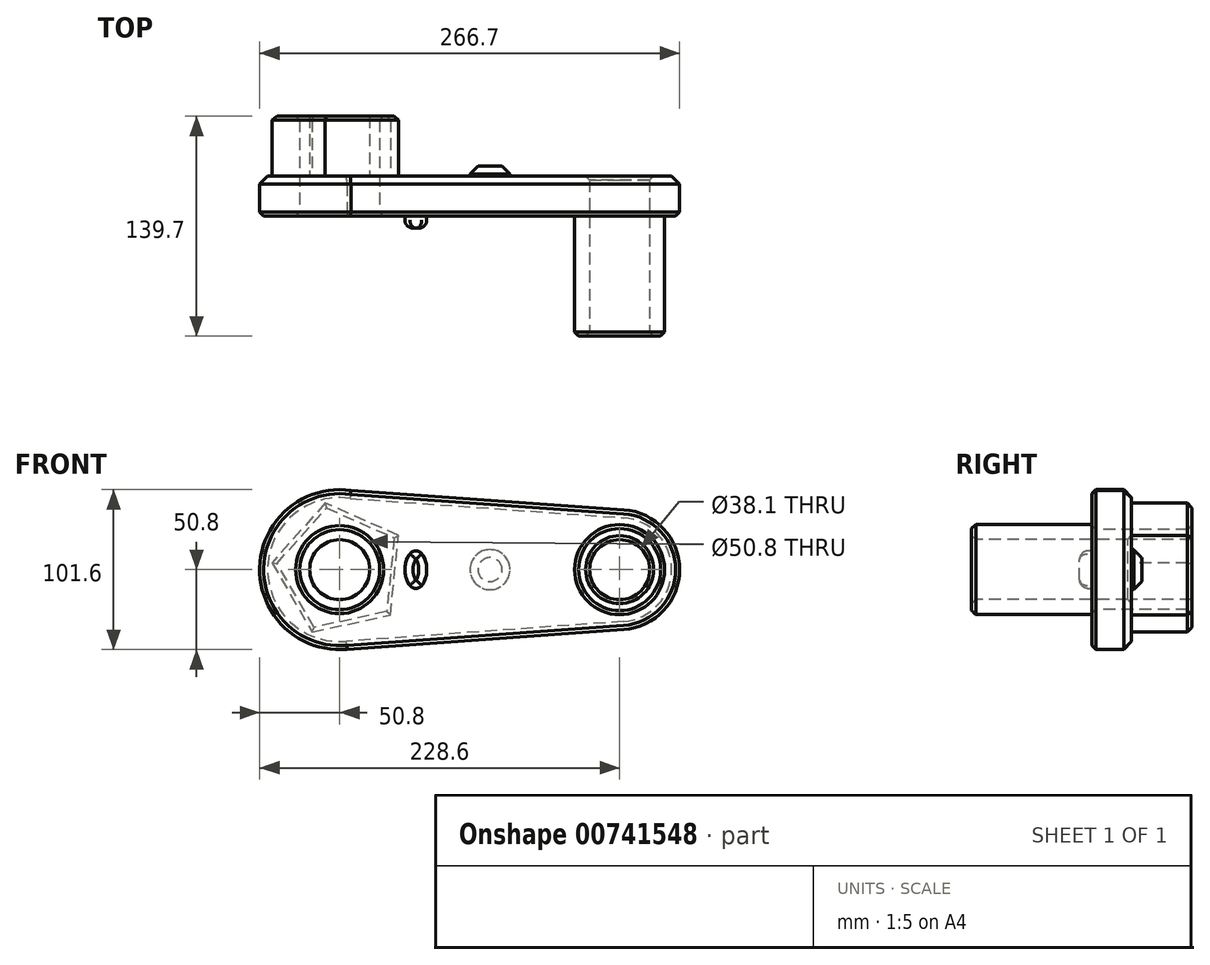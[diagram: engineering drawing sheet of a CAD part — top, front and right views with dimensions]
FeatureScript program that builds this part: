
annotation { "Feature Type Name" : "Feature", "Feature Type Description" : "" }
export const myFeature = defineFeature(function(context is Context, id is Id, definition is map)
    precondition{}
    {
        {
            var Q0;
            Q0=qCreatedBy(makeId("Front.planeOp"),FACE);
            var sketch = newSketch(context, id + "F0", { "sketchPlane" : qUnion([Q0])});
            skCircle(sketch, "E0", {"center": v(0, 0) * mm, "radius": 50.8 * mm});
            skCircle(sketch, "E1", {"center": v(177.8, 0) * mm, "radius": 38.1 * mm});
            skCircle(sketch, "E2", {"center": v(0, 0) * mm, "radius": 25.4 * mm});
            skCircle(sketch, "E3", {"center": v(177.8, 0) * mm, "radius": 19.05 * mm});
            skLineSegment(sketch, "E4", {"start": v(0, 50.8) * mm, "end": v(180.5, 38) * mm});
            skLineSegment(sketch, "E5", {"start": v(4.76, -50.58) * mm, "end": v(180.52, -38) * mm});
            skSolve(sketch);
        }
        {
            var Q0;
            Q0 = qSketchRegion(id + "F0", true);
            extrude(context, id + "F1", {"entities" : qUnion([Q0]), "oppositeDirection" : true, "depth" : 25.4 * mm, "offsetDistance" : 25.4 * mm});
        }
        {
            var Q0;
            Q0=makeQuery(id+"F1.opExtrude","CAP_FACE",FACE,{"disambiguationData":[OSD([sQuery(id+"F0.wireOp",EDGE,"E0"),sQuery(id+"F0.wireOp",EDGE,"E1"),sQuery(id+"F0.wireOp",EDGE,"E2"),sQuery(id+"F0.wireOp",EDGE,"E3"),sQuery(id+"F0.wireOp",EDGE,"E4"),sQuery(id+"F0.wireOp",EDGE,"E5")])],"isStart":true});
            var sketch = newSketch(context, id + "F2", { "sketchPlane" : qUnion([Q0])});
            skCircle(sketch, "E6", {"center": v(177.8, 0) * mm, "radius": 28.58 * mm});
            skCircle(sketch, "E7", {"center": v(177.8, 0) * mm, "radius": 19.05 * mm});
            skSolve(sketch);
        }
        {
            var Q0;
            Q0 = qSketchRegion(id + "F2", true);
            extrude(context, id + "F3", {"entities" : qUnion([Q0]), "operationType" : NewBodyOperationType.ADD, "depth" : 76.2 * mm, "offsetDistance" : 25.4 * mm});
        }
        {
            var Q0;
            Q0=makeQuery(id+"F1.opExtrude","CAP_FACE",FACE,{"disambiguationData":[OSD([sQuery(id+"F0.wireOp",EDGE,"E0"),sQuery(id+"F0.wireOp",EDGE,"E1"),sQuery(id+"F0.wireOp",EDGE,"E2"),sQuery(id+"F0.wireOp",EDGE,"E3"),sQuery(id+"F0.wireOp",EDGE,"E4"),sQuery(id+"F0.wireOp",EDGE,"E5")])],"isStart":false});
            var sketch = newSketch(context, id + "F4", { "sketchPlane" : qUnion([Q0])});
            skCircle(sketch, "E8.cCircle", {"center": v(0, 0) * mm, "radius": 43.21 * mm, "construction": true});
            skLineSegment(sketch, "E8.0", {"start": v(-32.22, -28.8) * mm, "end": v(-37.34, 21.75) * mm});
            skLineSegment(sketch, "E8.1", {"start": v(-37.34, 21.75) * mm, "end": v(9.14, 42.23) * mm});
            skLineSegment(sketch, "E8.2", {"start": v(9.14, 42.23) * mm, "end": v(43, 4.35) * mm});
            skLineSegment(sketch, "E8.3", {"start": v(43, 4.35) * mm, "end": v(17.43, -39.54) * mm});
            skLineSegment(sketch, "E8.4", {"start": v(17.43, -39.54) * mm, "end": v(-32.22, -28.8) * mm});
            skCircle(sketch, "E9", {"center": v(0, 0) * mm, "radius": 19.05 * mm});
            skSolve(sketch);
        }
        {
            var Q0;
            Q0=makeQuery(id+"F4.imprint","IMPRINT",FACE,{"disambiguationData":[TD([[makeQuery(id+"F4.imprint","IMPRINT",EDGE,{"derivedFrom":sQuery(id+"F4.wireOp",EDGE,"E9")}),1.0]])]});
            var Q1;
            Q1=makeQuery(id+"F4.imprint","IMPRINT",FACE,{"disambiguationData":[TD([[makeQuery(id+"F4.imprint","IMPRINT",EDGE,{"derivedFrom":sQuery(id+"F4.wireOp",EDGE,"E8.0")}),-1.0]])]});
            extrude(context, id + "F5", {"entities" : qUnion([Q0, Q1]), "operationType" : NewBodyOperationType.ADD, "depth" : 38.1 * mm, "offsetDistance" : 25.4 * mm});
        }
        {
            var Q0;
            Q0=makeQuery(id+"F1.opExtrude","CAP_EDGE",EDGE,{"disambiguationData":[OSD([sQuery(id+"F0.wireOp",EDGE,"E2")])],"isStart":true});
            var Q1;
            Q1=makeQuery(id+"F1.opExtrude","CAP_EDGE",EDGE,{"disambiguationData":[OSD([sQuery(id+"F0.wireOp",EDGE,"E4")])],"isStart":true});
            var Q2;
            Q2=makeQuery(id+"F1.opExtrude","CAP_EDGE",EDGE,{"disambiguationData":[OSD([sQuery(id+"F0.wireOp",EDGE,"E0")])],"isStart":true});
            var Q3;
            Q3=makeQuery(id+"F3.opExtrude","CAP_EDGE",EDGE,{"disambiguationData":[OSD([sQuery(id+"F2.wireOp",EDGE,"E6")])],"isStart":false});
            var Q4;
            Q4=makeQuery(id+"F3.opExtrude","CAP_EDGE",EDGE,{"disambiguationData":[OSD([sQuery(id+"F2.wireOp",EDGE,"E7")])],"isStart":false});
            var Q5;
            Q5=makeQuery(id+"F1.opExtrude","CAP_EDGE",EDGE,{"disambiguationData":[OSD([sQuery(id+"F0.wireOp",EDGE,"E1")])],"isStart":false});
            var Q6;
            Q6=makeQuery(id+"F1.opExtrude","CAP_EDGE",EDGE,{"disambiguationData":[OSD([sQuery(id+"F0.wireOp",EDGE,"E3")])],"isStart":false});
            var Q7;
            Q7=makeQuery(id+"F5.opExtrude","CAP_EDGE",EDGE,{"disambiguationData":[OSD([sQuery(id+"F0.wireOp",EDGE,"E2")])],"isStart":false});
            var Q8;
            Q8=makeQuery(id+"F5.opExtrude","CAP_EDGE",EDGE,{"disambiguationData":[OSD([sQuery(id+"F4.wireOp",EDGE,"E8.1")])],"isStart":false});
            var Q9;
            Q9=makeQuery(id+"F5.opExtrude","CAP_EDGE",EDGE,{"disambiguationData":[OSD([sQuery(id+"F4.wireOp",EDGE,"E8.0")])],"isStart":false});
            var Q10;
            Q10=makeQuery(id+"F5.opExtrude","CAP_EDGE",EDGE,{"disambiguationData":[OSD([sQuery(id+"F4.wireOp",EDGE,"E8.4")])],"isStart":false});
            var Q11;
            Q11=makeQuery(id+"F5.opExtrude","CAP_EDGE",EDGE,{"disambiguationData":[OSD([sQuery(id+"F4.wireOp",EDGE,"E8.3")])],"isStart":false});
            var Q12;
            Q12=makeQuery(id+"F5.opExtrude","CAP_EDGE",EDGE,{"disambiguationData":[OSD([sQuery(id+"F4.wireOp",EDGE,"E8.2")])],"isStart":false});
            chamfer(context, id + "F6", {"entities" : qUnion([Q0, Q1, Q2, Q3, Q4, Q5, Q6, Q7, Q8, Q9, Q10, Q11, Q12]), "width" : 2.54 * mm, "tangentPropagation" : true});
        }
        {
            var Q0;
            Q0=makeQuery(id+"F1.opExtrude","CAP_EDGE",EDGE,{"disambiguationData":[OSD([sQuery(id+"F0.wireOp",EDGE,"E0")])],"isStart":false});
            chamfer(context, id + "F7", {"entities" : qUnion([Q0]), "width" : 5.08 * mm, "tangentPropagation" : true});
        }
        {
            var Q0;
            Q0=qCreatedBy(makeId("Front.planeOp"),FACE);
            var sketch = newSketch(context, id + "F8", { "sketchPlane" : qUnion([Q0])});
            skEllipse(sketch, "E10", {"center": v(48.38, 0) * mm, "majorRadius": 11.92 * mm, "minorRadius": 6.9 * mm, "majorAxis": v(0, -1)});
            skSolve(sketch);
        }
        {
            var Q0;
            Q0 = qSketchRegion(id + "F8", true);
            extrude(context, id + "F9", {"entities" : qUnion([Q0]), "operationType" : NewBodyOperationType.ADD, "depth" : 7.62 * mm, "offsetDistance" : 25.4 * mm});
        }
        {
            var Q0;
            Q0=makeQuery(id+"F9.opExtrude","CAP_EDGE",EDGE,{"disambiguationData":[OSD([sQuery(id+"F8.wireOp",EDGE,"E10")])],"isStart":false});
            fillet(context, id + "F10", {"entities" : qUnion([Q0]), "radius" : 5.08 * mm, "tangentPropagation" : true, "allowEdgeOverflow" : false});
        }
        {
            var Q0;
            Q0=makeQuery(id+"F1.opExtrude","CAP_FACE",FACE,{"disambiguationData":[OSD([sQuery(id+"F0.wireOp",EDGE,"E0"),sQuery(id+"F0.wireOp",EDGE,"E1"),sQuery(id+"F0.wireOp",EDGE,"E2"),sQuery(id+"F0.wireOp",EDGE,"E3"),sQuery(id+"F0.wireOp",EDGE,"E4"),sQuery(id+"F0.wireOp",EDGE,"E5")])],"isStart":false});
            var sketch = newSketch(context, id + "F11", { "sketchPlane" : qUnion([Q0])});
            skCircle(sketch, "E11", {"center": v(-95.9, 0) * mm, "radius": 6.61 * mm});
            skSolve(sketch);
        }
        {
            var Q0;
            Q0=makeQuery(id+"F11.imprint","IMPRINT",FACE,{"disambiguationData":[TD([[makeQuery(id+"F11.imprint","IMPRINT",EDGE,{"derivedFrom":sQuery(id+"F11.wireOp",EDGE,"E11")}),-1.0]])]});
            var sketch = newSketch(context, id + "F12", { "sketchPlane" : qUnion([Q0])});
            skCircle(sketch, "E12", {"center": v(-95.49, 0) * mm, "radius": 12.7 * mm});
            skSolve(sketch);
        }
        {
            var Q0;
            Q0 = qSketchRegion(id + "F12", true);
            extrude(context, id + "F13", {"entities" : qUnion([Q0]), "operationType" : NewBodyOperationType.ADD, "depth" : 6.35 * mm, "offsetDistance" : 25.4 * mm});
        }
        {
            var Q0;
            Q0=makeQuery(id+"F13.opExtrude","CAP_EDGE",EDGE,{"disambiguationData":[OSD([sQuery(id+"F12.wireOp",EDGE,"E12")])],"isStart":false});
            chamfer(context, id + "F14", {"entities" : qUnion([Q0]), "width" : 5.08 * mm, "tangentPropagation" : true});
        }
    });
